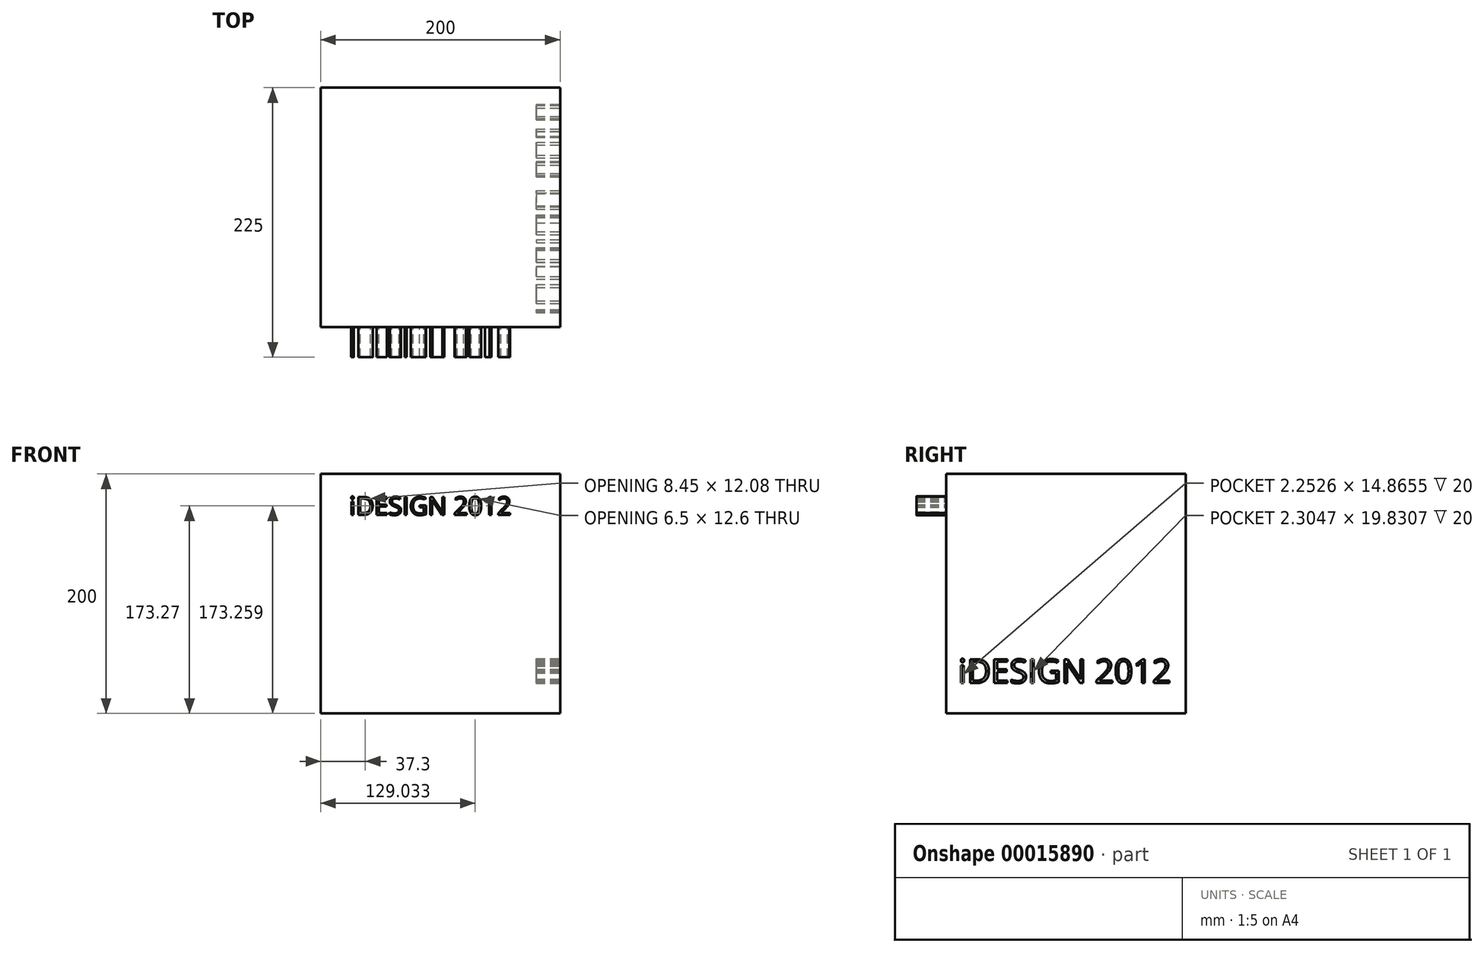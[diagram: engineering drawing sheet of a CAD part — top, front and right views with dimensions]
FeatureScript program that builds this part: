
annotation { "Feature Type Name" : "Feature", "Feature Type Description" : "" }
export const myFeature = defineFeature(function(context is Context, id is Id, definition is map)
    precondition{}
    {
        {
            var Q0;
            Q0=qCreatedBy(makeId("Front.planeOp"),FACE);
            var sketch = newSketch(context, id + "F0", { "sketchPlane" : qUnion([Q0])});
            skLineSegment(sketch, "E0.bottom", {"start": v(0, 0) * mm, "end": v(-200, 0) * mm});
            skLineSegment(sketch, "E0.top", {"start": v(0, 200) * mm, "end": v(-200, 200) * mm});
            skLineSegment(sketch, "E0.left", {"start": v(0, 0) * mm, "end": v(0, 200) * mm});
            skLineSegment(sketch, "E0.right", {"start": v(-200, 0) * mm, "end": v(-200, 200) * mm});
            skSolve(sketch);
        }
        {
            var Q0;
            Q0 = qSketchRegion(id + "F0", true);
            extrude(context, id + "F1", {"entities" : qUnion([Q0]), "depth" : 200 * mm});
        }
        {
            var Q0;
            Q0=makeQuery(id+"F1.opExtrude","SWEPT_FACE",FACE,{"disambiguationData":[OSD([sQuery(id+"F0.wireOp",EDGE,"E0.left")])]});
            var sketch = newSketch(context, id + "F2", { "sketchPlane" : qUnion([Q0])});
            skText(sketch, "E1", { "text": "iDESIGN 2012", "fontName": "OpenSans-Regular.ttf"});
            const initialGuessF2  = {"E1": [-0.19, 0.02533, 1, 0, 0.02]};
            skSetInitialGuess(sketch, initialGuessF2);
            skSolve(sketch);
        }
        {
            var Q0;
            Q0 = qSketchRegion(id + "F2", true);
            extrude(context, id + "F3", {"entities" : qUnion([Q0]), "operationType" : NewBodyOperationType.REMOVE, "oppositeDirection" : true, "depth" : 20 * mm});
        }
        {
            var Q0;
            Q0=makeQuery(id+"F1.opExtrude","CAP_FACE",FACE,{"disambiguationData":[OSD([sQuery(id+"F0.wireOp",EDGE,"E0.bottom"),sQuery(id+"F0.wireOp",EDGE,"E0.top"),sQuery(id+"F0.wireOp",EDGE,"E0.left"),sQuery(id+"F0.wireOp",EDGE,"E0.right")])],"isStart":false});
            var sketch = newSketch(context, id + "F4", { "sketchPlane" : qUnion([Q0])});
            skText(sketch, "E2", { "text": "iDESIGN 2012", "fontName": "OpenSans-Regular.ttf"});
            const initialGuessF4  = {"E2": [-0.17612, 0.1657, 1, 0, 0.01525]};
            skSetInitialGuess(sketch, initialGuessF4);
            skSolve(sketch);
        }
        {
            var Q0;
            Q0 = qSketchRegion(id + "F4", true);
            extrude(context, id + "F5", {"entities" : qUnion([Q0]), "depth" : 25 * mm});
        }
    });
